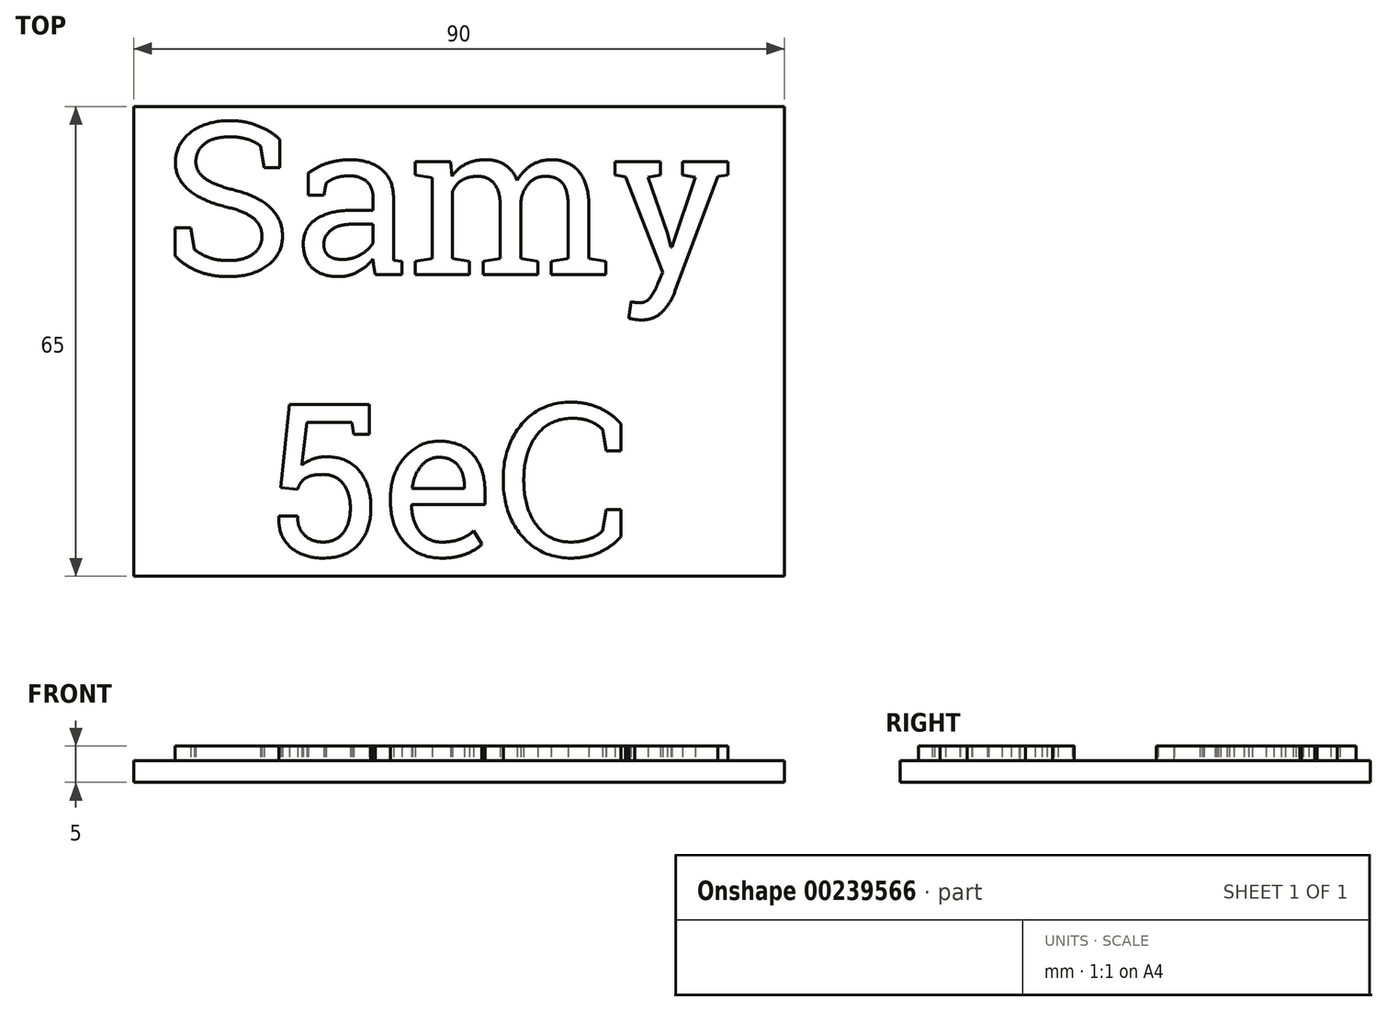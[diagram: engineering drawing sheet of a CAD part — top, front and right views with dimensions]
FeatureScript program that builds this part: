
annotation { "Feature Type Name" : "Feature", "Feature Type Description" : "" }
export const myFeature = defineFeature(function(context is Context, id is Id, definition is map)
    precondition{}
    {
        {
            var Q0;
            Q0=qCreatedBy(makeId("Top.planeOp"),FACE);
            var sketch = newSketch(context, id + "F0", { "sketchPlane" : qUnion([Q0])});
            skLineSegment(sketch, "E0.bottom", {"start": v(0, 0) * mm, "end": v(90, 0) * mm});
            skLineSegment(sketch, "E0.top", {"start": v(0, -65) * mm, "end": v(90, -65) * mm});
            skLineSegment(sketch, "E0.left", {"start": v(0, 0) * mm, "end": v(0, -65) * mm});
            skLineSegment(sketch, "E0.right", {"start": v(90, 0) * mm, "end": v(90, -65) * mm});
            skSolve(sketch);
        }
        {
            var Q0;
            Q0 = qSketchRegion(id + "F0", true);
            extrude(context, id + "F1", {"entities" : qUnion([Q0]), "depth" : 3 * mm});
        }
        {
            var Q0;
            Q0=makeQuery(id+"F1.opExtrude","CAP_FACE",FACE,{"disambiguationData":[OSD([sQuery(id+"F0.wireOp",EDGE,"E0.bottom"),sQuery(id+"F0.wireOp",EDGE,"E0.top"),sQuery(id+"F0.wireOp",EDGE,"E0.left"),sQuery(id+"F0.wireOp",EDGE,"E0.right")])],"isStart":false});
            var sketch = newSketch(context, id + "F2", { "sketchPlane" : qUnion([Q0])});
            skText(sketch, "E1", { "text": "Samy\n  5eC", "fontName": "RobotoSlab-Regular.ttf"});
            const initialGuessF2  = {"E1": [0.004, -0.02324, 1, 0, 0.02124]};
            skSetInitialGuess(sketch, initialGuessF2);
            skSolve(sketch);
        }
        {
            var Q0;
            Q0 = qSketchRegion(id + "F2", true);
            extrude(context, id + "F3", {"entities" : qUnion([Q0]), "operationType" : NewBodyOperationType.ADD, "depth" : 2 * mm});
        }
    });
